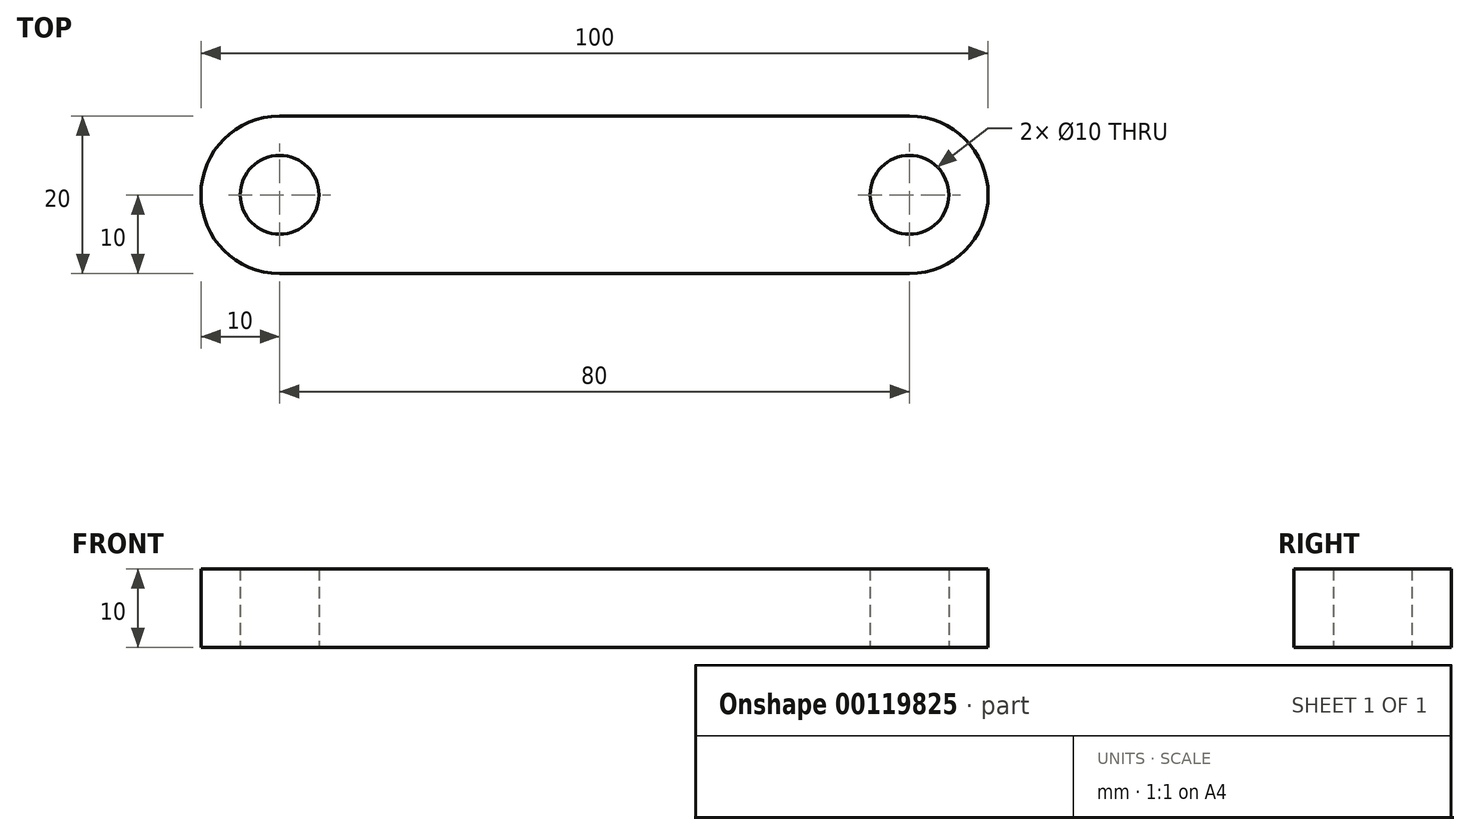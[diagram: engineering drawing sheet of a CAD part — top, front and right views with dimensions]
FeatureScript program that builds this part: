
annotation { "Feature Type Name" : "Feature", "Feature Type Description" : "" }
export const myFeature = defineFeature(function(context is Context, id is Id, definition is map)
    precondition{}
    {
        {
            var Q0;
            Q0=qCreatedBy(makeId("Top.planeOp"),FACE);
            var sketch = newSketch(context, id + "F0", { "sketchPlane" : qUnion([Q0])});
            skArc(sketch, "E0", {"start": v(-40, 10) * mm, "mid": v(-50, 0) * mm, "end": v(-40, -10) * mm});
            skArc(sketch, "E1", {"start": v(40, -10) * mm, "mid": v(50, 0) * mm, "end": v(40, 10) * mm});
            skLineSegment(sketch, "E2", {"start": v(-40, 10) * mm, "end": v(40, 10) * mm});
            skLineSegment(sketch, "E3", {"start": v(-40, -10) * mm, "end": v(40, -10) * mm});
            skCircle(sketch, "E4", {"center": v(-40, 0) * mm, "radius": 5 * mm});
            skCircle(sketch, "E5", {"center": v(40, 0) * mm, "radius": 5 * mm});
            skSolve(sketch);
        }
        {
            var Q0;
            Q0=qSketchRegion(id+"F0",true);
            extrude(context, id + "F1", {"entities" : qUnion([Q0]), "depth" : 10 * mm});
        }
    });
